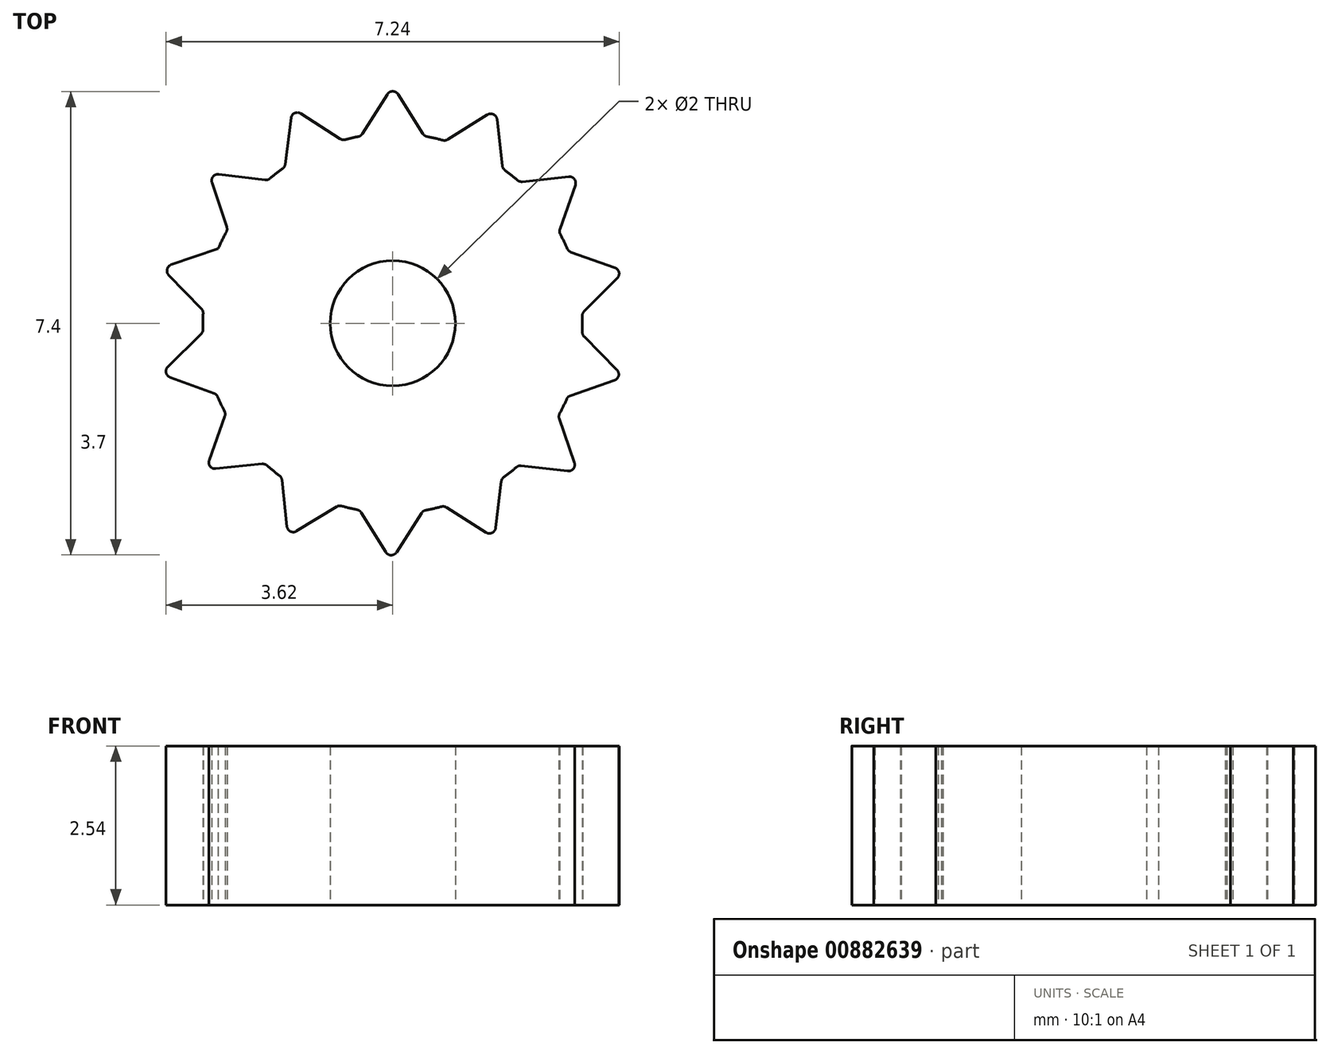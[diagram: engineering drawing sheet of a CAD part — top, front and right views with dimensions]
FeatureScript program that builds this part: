
annotation { "Feature Type Name" : "Feature", "Feature Type Description" : "" }
export const myFeature = defineFeature(function(context is Context, id is Id, definition is map)
    precondition{}
    {
        {
            var Q0;
            Q0=qCreatedBy(makeId("Top.planeOp"),FACE);
            var sketch = newSketch(context, id + "F0", { "sketchPlane" : qUnion([Q0])});
            skArc(sketch, "E0.0", {"start": v(-0.5, 2.99) * mm, "mid": v(0, -3.03) * mm, "end": v(0.5, 2.99) * mm});
            skPoint(sketch, "E1.start.orphan", {"position": v(0, 3.8) * mm});
            skPoint(sketch, "E2", {"position": v(0, 3.41) * mm});
            skLineSegment(sketch, "E3", {"start": v(-0.5, 2.99) * mm, "end": v(0, 3.8) * mm});
            skLineSegment(sketch, "E4", {"start": v(0, 3.8) * mm, "end": v(0.5, 2.99) * mm});
            skPoint(sketch, "E5.end.orphan", {"position": v(-0.5, 3.6) * mm});
            skPoint(sketch, "E6.end.orphan", {"position": v(0.5, 3.6) * mm});
            skPoint(sketch, "E7.orphan", {"position": v(0, 6.83) * mm});
            skCircle(sketch, "E8", {"center": v(0, 0) * mm, "radius": 1 * mm});
            skLineSegment(sketch, "E9.1.0", {"start": v(0.84, 2.91) * mm, "end": v(1.65, 3.42) * mm});
            skLineSegment(sketch, "E9.1.1", {"start": v(1.65, 3.42) * mm, "end": v(1.76, 2.47) * mm});
            skLineSegment(sketch, "E9.2.0", {"start": v(2.02, 2.26) * mm, "end": v(2.97, 2.36) * mm});
            skLineSegment(sketch, "E9.2.1", {"start": v(2.97, 2.36) * mm, "end": v(2.66, 1.46) * mm});
            skLineSegment(sketch, "E9.3.0", {"start": v(2.8, 1.15) * mm, "end": v(3.7, 0.83) * mm});
            skLineSegment(sketch, "E9.3.1", {"start": v(3.7, 0.83) * mm, "end": v(3.03, 0.16) * mm});
            skLineSegment(sketch, "E9.4.0", {"start": v(3.03, -0.18) * mm, "end": v(3.7, -0.86) * mm});
            skLineSegment(sketch, "E9.4.1", {"start": v(3.7, -0.86) * mm, "end": v(2.8, -1.17) * mm});
            skLineSegment(sketch, "E9.5.0", {"start": v(2.65, -1.48) * mm, "end": v(2.95, -2.38) * mm});
            skLineSegment(sketch, "E9.5.1", {"start": v(2.95, -2.38) * mm, "end": v(2, -2.27) * mm});
            skLineSegment(sketch, "E9.6.0", {"start": v(1.74, -2.48) * mm, "end": v(1.63, -3.43) * mm});
            skLineSegment(sketch, "E9.6.1", {"start": v(1.63, -3.43) * mm, "end": v(0.82, -2.92) * mm});
            skLineSegment(sketch, "E9.7.0", {"start": v(0.49, -3) * mm, "end": v(-0.03, -3.8) * mm});
            skLineSegment(sketch, "E9.7.1", {"start": v(-0.03, -3.8) * mm, "end": v(-0.53, -2.98) * mm});
            skLineSegment(sketch, "E9.8.0", {"start": v(-0.86, -2.9) * mm, "end": v(-1.67, -3.4) * mm});
            skLineSegment(sketch, "E9.8.1", {"start": v(-1.67, -3.4) * mm, "end": v(-1.77, -2.46) * mm});
            skLineSegment(sketch, "E9.9.0", {"start": v(-2.04, -2.24) * mm, "end": v(-2.99, -2.34) * mm});
            skLineSegment(sketch, "E9.9.1", {"start": v(-2.99, -2.34) * mm, "end": v(-2.67, -1.44) * mm});
            skLineSegment(sketch, "E9.10.0", {"start": v(-2.81, -1.13) * mm, "end": v(-3.7, -0.8) * mm});
            skLineSegment(sketch, "E9.10.1", {"start": v(-3.7, -0.8) * mm, "end": v(-3.03, -0.14) * mm});
            skLineSegment(sketch, "E9.11.0", {"start": v(-3.02, 0.2) * mm, "end": v(-3.69, 0.88) * mm});
            skLineSegment(sketch, "E9.11.1", {"start": v(-3.69, 0.88) * mm, "end": v(-2.79, 1.19) * mm});
            skLineSegment(sketch, "E9.12.0", {"start": v(-2.64, 1.5) * mm, "end": v(-2.94, 2.4) * mm});
            skLineSegment(sketch, "E9.12.1", {"start": v(-2.94, 2.4) * mm, "end": v(-2, 2.28) * mm});
            skLineSegment(sketch, "E9.13.0", {"start": v(-1.72, 2.5) * mm, "end": v(-1.6, 3.44) * mm});
            skLineSegment(sketch, "E9.13.1", {"start": v(-1.6, 3.44) * mm, "end": v(-0.8, 2.92) * mm});
            skLineSegment(sketch, "E9.anchor1", {"start": v(0, 0) * mm, "end": v(-0.5, 2.99) * mm, "construction": true});
            skLineSegment(sketch, "E9.anchor2", {"start": v(0, 0) * mm, "end": v(-1.72, 2.5) * mm, "construction": true});
            skSolve(sketch);
        }
        {
            var Q0;
            {var subQ18=sQuery(id+"F0.wireOp",EDGE,"E3");Q0=makeQuery(id+"F0.imprint","IMPRINT",FACE,{"disambiguationData":[TD([[makeQuery(id+"F0.imprint","IMPRINT",EDGE,{"derivedFrom":subQ18}),-1.0]])]});}
            var Q1;
            {var subQ0=sQuery(id+"F0.wireOp",EDGE,"E9.1.0");Q1=makeQuery(id+"F0.imprint","IMPRINT",FACE,{"disambiguationData":[TD([[makeQuery(id+"F0.imprint","IMPRINT",EDGE,{"derivedFrom":subQ0}),-1.0]])]});}
            var Q2;
            {var subQ0=sQuery(id+"F0.wireOp",EDGE,"E9.13.0");Q2=makeQuery(id+"F0.imprint","IMPRINT",FACE,{"disambiguationData":[TD([[makeQuery(id+"F0.imprint","IMPRINT",EDGE,{"derivedFrom":subQ0}),-1.0]])]});}
            var Q3;
            {var subQ0=sQuery(id+"F0.wireOp",EDGE,"E9.12.0");Q3=makeQuery(id+"F0.imprint","IMPRINT",FACE,{"disambiguationData":[TD([[makeQuery(id+"F0.imprint","IMPRINT",EDGE,{"derivedFrom":subQ0}),-1.0]])]});}
            var Q4;
            {var subQ0=sQuery(id+"F0.wireOp",EDGE,"E9.11.0");Q4=makeQuery(id+"F0.imprint","IMPRINT",FACE,{"disambiguationData":[TD([[makeQuery(id+"F0.imprint","IMPRINT",EDGE,{"derivedFrom":subQ0}),-1.0]])]});}
            var Q5;
            {var subQ0=sQuery(id+"F0.wireOp",EDGE,"E9.10.0");Q5=makeQuery(id+"F0.imprint","IMPRINT",FACE,{"disambiguationData":[TD([[makeQuery(id+"F0.imprint","IMPRINT",EDGE,{"derivedFrom":subQ0}),-1.0]])]});}
            var Q6;
            {var subQ0=sQuery(id+"F0.wireOp",EDGE,"E9.9.0");Q6=makeQuery(id+"F0.imprint","IMPRINT",FACE,{"disambiguationData":[TD([[makeQuery(id+"F0.imprint","IMPRINT",EDGE,{"derivedFrom":subQ0}),-1.0]])]});}
            var Q7;
            {var subQ0=sQuery(id+"F0.wireOp",EDGE,"E9.8.0");Q7=makeQuery(id+"F0.imprint","IMPRINT",FACE,{"disambiguationData":[TD([[makeQuery(id+"F0.imprint","IMPRINT",EDGE,{"derivedFrom":subQ0}),-1.0]])]});}
            var Q8;
            {var subQ0=sQuery(id+"F0.wireOp",EDGE,"E9.7.0");Q8=makeQuery(id+"F0.imprint","IMPRINT",FACE,{"disambiguationData":[TD([[makeQuery(id+"F0.imprint","IMPRINT",EDGE,{"derivedFrom":subQ0}),-1.0]])]});}
            var Q9;
            {var subQ0=sQuery(id+"F0.wireOp",EDGE,"E9.6.0");Q9=makeQuery(id+"F0.imprint","IMPRINT",FACE,{"disambiguationData":[TD([[makeQuery(id+"F0.imprint","IMPRINT",EDGE,{"derivedFrom":subQ0}),-1.0]])]});}
            var Q10;
            {var subQ0=sQuery(id+"F0.wireOp",EDGE,"E9.5.0");Q10=makeQuery(id+"F0.imprint","IMPRINT",FACE,{"disambiguationData":[TD([[makeQuery(id+"F0.imprint","IMPRINT",EDGE,{"derivedFrom":subQ0}),-1.0]])]});}
            var Q11;
            {var subQ0=sQuery(id+"F0.wireOp",EDGE,"E9.4.0");Q11=makeQuery(id+"F0.imprint","IMPRINT",FACE,{"disambiguationData":[TD([[makeQuery(id+"F0.imprint","IMPRINT",EDGE,{"derivedFrom":subQ0}),-1.0]])]});}
            var Q12;
            {var subQ0=sQuery(id+"F0.wireOp",EDGE,"E9.3.0");Q12=makeQuery(id+"F0.imprint","IMPRINT",FACE,{"disambiguationData":[TD([[makeQuery(id+"F0.imprint","IMPRINT",EDGE,{"derivedFrom":subQ0}),-1.0]])]});}
            var Q13;
            {var subQ0=sQuery(id+"F0.wireOp",EDGE,"E9.2.0");Q13=makeQuery(id+"F0.imprint","IMPRINT",FACE,{"disambiguationData":[TD([[makeQuery(id+"F0.imprint","IMPRINT",EDGE,{"derivedFrom":subQ0}),-1.0]])]});}
            extrude(context, id + "F1", {"entities" : qUnion([Q0, Q1, Q2, Q3, Q4, Q5, Q6, Q7, Q8, Q9, Q10, Q11, Q12, Q13]), "depth" : 2.54 * mm, "offsetDistance" : 25.4 * mm});
        }
        {
            var Q0;
            Q0=makeQuery(id+"F1.opExtrude","SWEPT_EDGE",EDGE,{"disambiguationData":[OSD([sQuery(id+"F0.wireOp",EDGE,"E3"),sQuery(id+"F0.wireOp",EDGE,"E4")])]});
            var Q1;
            Q1=makeQuery(id+"F1.opExtrude","SWEPT_EDGE",EDGE,{"disambiguationData":[OSD([sQuery(id+"F0.wireOp",EDGE,"E9.13.0"),sQuery(id+"F0.wireOp",EDGE,"E9.13.1")])]});
            var Q2;
            Q2=makeQuery(id+"F1.opExtrude","SWEPT_EDGE",EDGE,{"disambiguationData":[OSD([sQuery(id+"F0.wireOp",EDGE,"E9.12.0"),sQuery(id+"F0.wireOp",EDGE,"E9.12.1")])]});
            var Q3;
            Q3=makeQuery(id+"F1.opExtrude","SWEPT_EDGE",EDGE,{"disambiguationData":[OSD([sQuery(id+"F0.wireOp",EDGE,"E9.11.0"),sQuery(id+"F0.wireOp",EDGE,"E9.11.1")])]});
            var Q4;
            Q4=makeQuery(id+"F1.opExtrude","SWEPT_EDGE",EDGE,{"disambiguationData":[OSD([sQuery(id+"F0.wireOp",EDGE,"E9.10.0"),sQuery(id+"F0.wireOp",EDGE,"E9.10.1")])]});
            var Q5;
            Q5=makeQuery(id+"F1.opExtrude","SWEPT_EDGE",EDGE,{"disambiguationData":[OSD([sQuery(id+"F0.wireOp",EDGE,"E9.9.0"),sQuery(id+"F0.wireOp",EDGE,"E9.9.1")])]});
            var Q6;
            Q6=makeQuery(id+"F1.opExtrude","SWEPT_EDGE",EDGE,{"disambiguationData":[OSD([sQuery(id+"F0.wireOp",EDGE,"E9.8.0"),sQuery(id+"F0.wireOp",EDGE,"E9.8.1")])]});
            var Q7;
            Q7=makeQuery(id+"F1.opExtrude","SWEPT_EDGE",EDGE,{"disambiguationData":[OSD([sQuery(id+"F0.wireOp",EDGE,"E9.7.0"),sQuery(id+"F0.wireOp",EDGE,"E9.7.1")])]});
            var Q8;
            Q8=makeQuery(id+"F1.opExtrude","SWEPT_EDGE",EDGE,{"disambiguationData":[OSD([sQuery(id+"F0.wireOp",EDGE,"E9.6.0"),sQuery(id+"F0.wireOp",EDGE,"E9.6.1")])]});
            var Q9;
            Q9=makeQuery(id+"F1.opExtrude","SWEPT_EDGE",EDGE,{"disambiguationData":[OSD([sQuery(id+"F0.wireOp",EDGE,"E9.5.0"),sQuery(id+"F0.wireOp",EDGE,"E9.5.1")])]});
            var Q10;
            Q10=makeQuery(id+"F1.opExtrude","SWEPT_EDGE",EDGE,{"disambiguationData":[OSD([sQuery(id+"F0.wireOp",EDGE,"E9.4.0"),sQuery(id+"F0.wireOp",EDGE,"E9.4.1")])]});
            var Q11;
            Q11=makeQuery(id+"F1.opExtrude","SWEPT_EDGE",EDGE,{"disambiguationData":[OSD([sQuery(id+"F0.wireOp",EDGE,"E9.3.0"),sQuery(id+"F0.wireOp",EDGE,"E9.3.1")])]});
            var Q12;
            Q12=makeQuery(id+"F1.opExtrude","SWEPT_EDGE",EDGE,{"disambiguationData":[OSD([sQuery(id+"F0.wireOp",EDGE,"E9.2.0"),sQuery(id+"F0.wireOp",EDGE,"E9.2.1")])]});
            var Q13;
            Q13=makeQuery(id+"F1.opExtrude","SWEPT_EDGE",EDGE,{"disambiguationData":[OSD([sQuery(id+"F0.wireOp",EDGE,"E9.1.0"),sQuery(id+"F0.wireOp",EDGE,"E9.1.1")])]});
            var Q14;
            Q14=makeQuery(id+"F1.opExtrude","SWEPT_EDGE",EDGE,{"disambiguationData":[OSD([sQuery(id+"F0.wireOp",EDGE,"E0.0"),sQuery(id+"F0.wireOp",EDGE,"E4")])]});
            var Q15;
            Q15=makeQuery(id+"F1.opExtrude","SWEPT_EDGE",EDGE,{"disambiguationData":[OSD([sQuery(id+"F0.wireOp",EDGE,"E0.0"),sQuery(id+"F0.wireOp",EDGE,"E9.1.0")])]});
            var Q16;
            Q16=makeQuery(id+"F1.opExtrude","SWEPT_EDGE",EDGE,{"disambiguationData":[OSD([sQuery(id+"F0.wireOp",EDGE,"E0.0"),sQuery(id+"F0.wireOp",EDGE,"E9.1.1")])]});
            var Q17;
            Q17=makeQuery(id+"F1.opExtrude","SWEPT_EDGE",EDGE,{"disambiguationData":[OSD([sQuery(id+"F0.wireOp",EDGE,"E0.0"),sQuery(id+"F0.wireOp",EDGE,"E9.2.0")])]});
            var Q18;
            Q18=makeQuery(id+"F1.opExtrude","SWEPT_EDGE",EDGE,{"disambiguationData":[OSD([sQuery(id+"F0.wireOp",EDGE,"E0.0"),sQuery(id+"F0.wireOp",EDGE,"E9.2.1")])]});
            var Q19;
            Q19=makeQuery(id+"F1.opExtrude","SWEPT_EDGE",EDGE,{"disambiguationData":[OSD([sQuery(id+"F0.wireOp",EDGE,"E0.0"),sQuery(id+"F0.wireOp",EDGE,"E9.3.0")])]});
            var Q20;
            Q20=makeQuery(id+"F1.opExtrude","SWEPT_EDGE",EDGE,{"disambiguationData":[OSD([sQuery(id+"F0.wireOp",EDGE,"E0.0"),sQuery(id+"F0.wireOp",EDGE,"E9.3.1")])]});
            var Q21;
            Q21=makeQuery(id+"F1.opExtrude","SWEPT_EDGE",EDGE,{"disambiguationData":[OSD([sQuery(id+"F0.wireOp",EDGE,"E0.0"),sQuery(id+"F0.wireOp",EDGE,"E9.4.0")])]});
            var Q22;
            Q22=makeQuery(id+"F1.opExtrude","SWEPT_EDGE",EDGE,{"disambiguationData":[OSD([sQuery(id+"F0.wireOp",EDGE,"E0.0"),sQuery(id+"F0.wireOp",EDGE,"E9.4.1")])]});
            var Q23;
            Q23=makeQuery(id+"F1.opExtrude","SWEPT_EDGE",EDGE,{"disambiguationData":[OSD([sQuery(id+"F0.wireOp",EDGE,"E0.0"),sQuery(id+"F0.wireOp",EDGE,"E9.5.0")])]});
            var Q24;
            Q24=makeQuery(id+"F1.opExtrude","SWEPT_EDGE",EDGE,{"disambiguationData":[OSD([sQuery(id+"F0.wireOp",EDGE,"E0.0"),sQuery(id+"F0.wireOp",EDGE,"E9.5.1")])]});
            var Q25;
            Q25=makeQuery(id+"F1.opExtrude","SWEPT_EDGE",EDGE,{"disambiguationData":[OSD([sQuery(id+"F0.wireOp",EDGE,"E0.0"),sQuery(id+"F0.wireOp",EDGE,"E9.6.0")])]});
            var Q26;
            Q26=makeQuery(id+"F1.opExtrude","SWEPT_EDGE",EDGE,{"disambiguationData":[OSD([sQuery(id+"F0.wireOp",EDGE,"E0.0"),sQuery(id+"F0.wireOp",EDGE,"E9.6.1")])]});
            var Q27;
            Q27=makeQuery(id+"F1.opExtrude","SWEPT_EDGE",EDGE,{"disambiguationData":[OSD([sQuery(id+"F0.wireOp",EDGE,"E0.0"),sQuery(id+"F0.wireOp",EDGE,"E9.7.0")])]});
            var Q28;
            Q28=makeQuery(id+"F1.opExtrude","SWEPT_EDGE",EDGE,{"disambiguationData":[OSD([sQuery(id+"F0.wireOp",EDGE,"E0.0"),sQuery(id+"F0.wireOp",EDGE,"E9.7.1")])]});
            var Q29;
            Q29=makeQuery(id+"F1.opExtrude","SWEPT_EDGE",EDGE,{"disambiguationData":[OSD([sQuery(id+"F0.wireOp",EDGE,"E0.0"),sQuery(id+"F0.wireOp",EDGE,"E9.8.0")])]});
            var Q30;
            Q30=makeQuery(id+"F1.opExtrude","SWEPT_EDGE",EDGE,{"disambiguationData":[OSD([sQuery(id+"F0.wireOp",EDGE,"E0.0"),sQuery(id+"F0.wireOp",EDGE,"E9.8.1")])]});
            var Q31;
            Q31=makeQuery(id+"F1.opExtrude","SWEPT_EDGE",EDGE,{"disambiguationData":[OSD([sQuery(id+"F0.wireOp",EDGE,"E0.0"),sQuery(id+"F0.wireOp",EDGE,"E9.9.0")])]});
            var Q32;
            Q32=makeQuery(id+"F1.opExtrude","SWEPT_EDGE",EDGE,{"disambiguationData":[OSD([sQuery(id+"F0.wireOp",EDGE,"E0.0"),sQuery(id+"F0.wireOp",EDGE,"E9.9.1")])]});
            var Q33;
            Q33=makeQuery(id+"F1.opExtrude","SWEPT_EDGE",EDGE,{"disambiguationData":[OSD([sQuery(id+"F0.wireOp",EDGE,"E0.0"),sQuery(id+"F0.wireOp",EDGE,"E9.10.0")])]});
            var Q34;
            Q34=makeQuery(id+"F1.opExtrude","SWEPT_EDGE",EDGE,{"disambiguationData":[OSD([sQuery(id+"F0.wireOp",EDGE,"E0.0"),sQuery(id+"F0.wireOp",EDGE,"E9.10.1")])]});
            var Q35;
            Q35=makeQuery(id+"F1.opExtrude","SWEPT_EDGE",EDGE,{"disambiguationData":[OSD([sQuery(id+"F0.wireOp",EDGE,"E0.0"),sQuery(id+"F0.wireOp",EDGE,"E9.11.0")])]});
            var Q36;
            Q36=makeQuery(id+"F1.opExtrude","SWEPT_EDGE",EDGE,{"disambiguationData":[OSD([sQuery(id+"F0.wireOp",EDGE,"E0.0"),sQuery(id+"F0.wireOp",EDGE,"E9.12.0")])]});
            var Q37;
            Q37=makeQuery(id+"F1.opExtrude","SWEPT_EDGE",EDGE,{"disambiguationData":[OSD([sQuery(id+"F0.wireOp",EDGE,"E0.0"),sQuery(id+"F0.wireOp",EDGE,"E9.13.0")])]});
            var Q38;
            Q38=makeQuery(id+"F1.opExtrude","SWEPT_EDGE",EDGE,{"disambiguationData":[OSD([sQuery(id+"F0.wireOp",EDGE,"E0.0"),sQuery(id+"F0.wireOp",EDGE,"E9.12.1")])]});
            var Q39;
            Q39=makeQuery(id+"F1.opExtrude","SWEPT_EDGE",EDGE,{"disambiguationData":[OSD([sQuery(id+"F0.wireOp",EDGE,"E0.0"),sQuery(id+"F0.wireOp",EDGE,"E9.13.1")])]});
            var Q40;
            Q40=makeQuery(id+"F1.opExtrude","SWEPT_EDGE",EDGE,{"disambiguationData":[OSD([sQuery(id+"F0.wireOp",EDGE,"E0.0"),sQuery(id+"F0.wireOp",EDGE,"E3")])]});
            fillet(context, id + "F2", {"entities" : qUnion([Q0, Q1, Q2, Q3, Q4, Q5, Q6, Q7, Q8, Q9, Q10, Q11, Q12, Q13, Q14, Q15, Q16, Q17, Q18, Q19, Q20, Q21, Q22, Q23, Q24, Q25, Q26, Q27, Q28, Q29, Q30, Q31, Q32, Q33, Q34, Q35, Q36, Q37, Q38, Q39, Q40]), "radius" : 0.1 * mm, "tangentPropagation" : true, "allowEdgeOverflow" : false});
        }
    });
